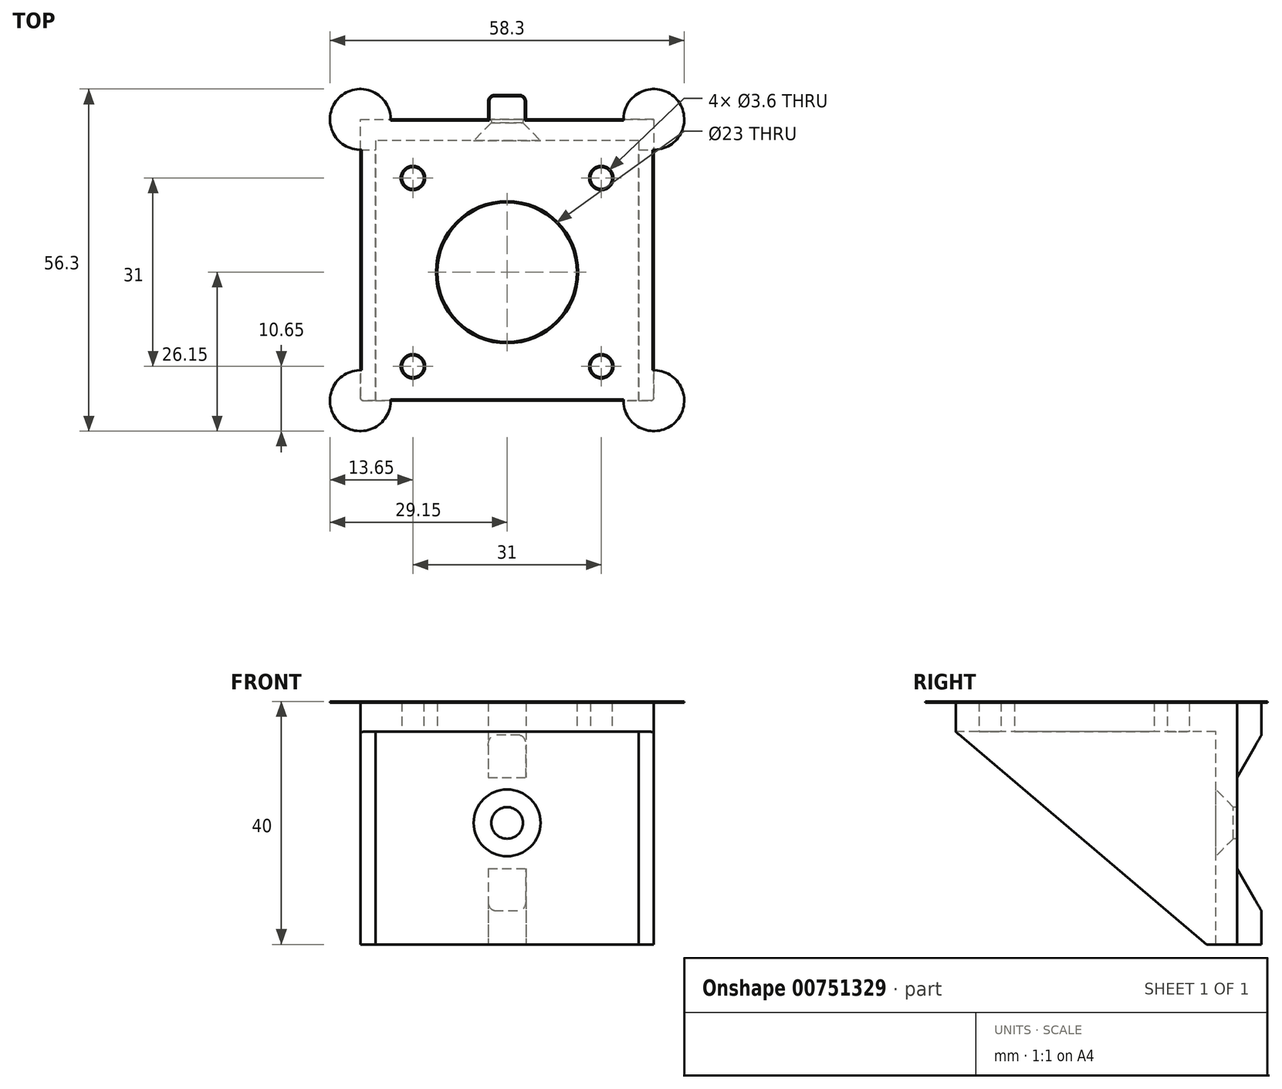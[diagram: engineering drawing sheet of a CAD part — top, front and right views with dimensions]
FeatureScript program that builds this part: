
annotation { "Feature Type Name" : "Feature", "Feature Type Description" : "" }
export const myFeature = defineFeature(function(context is Context, id is Id, definition is map)
    precondition{}
    {
        {
            var Q0;
            Q0=qCreatedBy(makeId("Top.planeOp"),FACE);
            var sketch = newSketch(context, id + "F0", { "sketchPlane" : qUnion([Q0])});
            skLineSegment(sketch, "E0.bottom", {"start": v(15.5, 15.5) * mm, "end": v(-15.5, 15.5) * mm, "construction": true});
            skLineSegment(sketch, "E0.top", {"start": v(15.5, -15.5) * mm, "end": v(-15.5, -15.5) * mm, "construction": true});
            skLineSegment(sketch, "E0.left", {"start": v(15.5, 15.5) * mm, "end": v(15.5, -15.5) * mm, "construction": true});
            skLineSegment(sketch, "E0.right", {"start": v(-15.5, 15.5) * mm, "end": v(-15.5, -15.5) * mm, "construction": true});
            skPoint(sketch, "E0.middle", {"position": v(0, 0) * mm});
            skCircle(sketch, "E1", {"center": v(15.5, 15.5) * mm, "radius": 1.5 * mm, "construction": true});
            skCircle(sketch, "E2", {"center": v(15.5, -15.5) * mm, "radius": 1.5 * mm, "construction": true});
            skCircle(sketch, "E3", {"center": v(-15.5, -15.5) * mm, "radius": 1.5 * mm, "construction": true});
            skCircle(sketch, "E4", {"center": v(-15.5, 15.5) * mm, "radius": 1.5 * mm, "construction": true});
            skLineSegment(sketch, "E5.bottom", {"start": v(21.15, 21.15) * mm, "end": v(-21.15, 21.15) * mm, "construction": true});
            skLineSegment(sketch, "E5.top", {"start": v(21.15, -21.15) * mm, "end": v(-21.15, -21.15) * mm, "construction": true});
            skLineSegment(sketch, "E5.left", {"start": v(21.15, 21.15) * mm, "end": v(21.15, -21.15) * mm, "construction": true});
            skLineSegment(sketch, "E5.right", {"start": v(-21.15, 21.15) * mm, "end": v(-21.15, -21.15) * mm, "construction": true});
            skCircle(sketch, "E6", {"center": v(0, 0) * mm, "radius": 11 * mm, "construction": true});
            skSolve(sketch);
        }
        {
            var Q0;
            Q0=qCreatedBy(makeId("Top.planeOp"),FACE);
            var sketch = newSketch(context, id + "F1", { "sketchPlane" : qUnion([Q0])});
            skPoint(sketch, "E7.middle", {"position": v(0, 0) * mm});
            skLineSegment(sketch, "E8.0", {"start": v(-21.15, 21.15) * mm, "end": v(-21.15, -21.15) * mm, "construction": true});
            skLineSegment(sketch, "E9.0", {"start": v(21.15, 21.15) * mm, "end": v(-21.15, 21.15) * mm, "construction": true});
            skLineSegment(sketch, "E10.0", {"start": v(21.15, 21.15) * mm, "end": v(21.15, -21.15) * mm, "construction": true});
            skLineSegment(sketch, "E11.0", {"start": v(21.15, -21.15) * mm, "end": v(-21.15, -21.15) * mm, "construction": true});
            skLineSegment(sketch, "E12", {"start": v(-24.15, -21.15) * mm, "end": v(24.15, -21.15) * mm});
            skLineSegment(sketch, "E13", {"start": v(-24.15, -21.15) * mm, "end": v(-24.15, 25.15) * mm});
            skLineSegment(sketch, "E14", {"start": v(-24.15, 25.15) * mm, "end": v(24.15, 25.15) * mm});
            skLineSegment(sketch, "E15", {"start": v(24.15, 25.15) * mm, "end": v(24.15, -21.15) * mm});
            skLineSegment(sketch, "E16", {"start": v(-3.1, 25.15) * mm, "end": v(-3.1, 29.15) * mm});
            skLineSegment(sketch, "E17", {"start": v(-3.1, 29.15) * mm, "end": v(3.1, 29.15) * mm});
            skLineSegment(sketch, "E18", {"start": v(3.1, 29.15) * mm, "end": v(3.1, 25.15) * mm});
            skSolve(sketch);
        }
        {
            var Q0;
            Q0 = qSketchRegion(id + "F1", true);
            extrude(context, id + "F2", {"entities" : qUnion([Q0]), "depth" : 5 * mm, "offsetDistance" : 25 * mm, "hasSecondDirection" : true, "secondDirectionOppositeDirection" : true, "secondDirectionDepth" : 35 * mm});
        }
        {
            var Q0;
            Q0=makeQuery(id+"F2.opExtrude","SWEPT_EDGE",EDGE,{"disambiguationData":[OSD([sQuery(id+"F1.wireOp",EDGE,"E16"),sQuery(id+"F1.wireOp",EDGE,"E17")])]});
            var Q1;
            Q1=makeQuery(id+"F2.opExtrude","SWEPT_EDGE",EDGE,{"disambiguationData":[OSD([sQuery(id+"F1.wireOp",EDGE,"E17"),sQuery(id+"F1.wireOp",EDGE,"E18")])]});
            fillet(context, id + "F3", {"entities" : qUnion([Q0, Q1]), "radius" : 1 * mm, "allowEdgeOverflow" : false});
        }
        {
            var Q0;
            Q0=qCreatedBy(makeId("Right.planeOp"),FACE);
            var sketch = newSketch(context, id + "F4", { "sketchPlane" : qUnion([Q0])});
            skLineSegment(sketch, "E19.0.0", {"start": v(25.15, -35) * mm, "end": v(-21.15, -35) * mm, "construction": true});
            skLineSegment(sketch, "E19.0.1", {"start": v(-21.15, -35) * mm, "end": v(-21.15, 5) * mm, "construction": true});
            skLineSegment(sketch, "E19.0.2", {"start": v(-21.15, 5) * mm, "end": v(25.15, 5) * mm, "construction": true});
            skLineSegment(sketch, "E19.0.3", {"start": v(25.15, 5) * mm, "end": v(25.15, -35) * mm, "construction": true});
            skLineSegment(sketch, "E20", {"start": v(-21.15, 0) * mm, "end": v(20.15, -35) * mm});
            skLineSegment(sketch, "E21", {"start": v(20.15, -35) * mm, "end": v(-21.15, -35) * mm});
            skLineSegment(sketch, "E22", {"start": v(-21.15, 0) * mm, "end": v(-21.15, -35) * mm});
            skPoint(sketch, "E23", {"position": v(25.15, -15) * mm});
            skLineSegment(sketch, "E24", {"start": v(25.15, -7.5) * mm, "end": v(25.15, -22.5) * mm});
            skLineSegment(sketch, "E25", {"start": v(25.15, -7.5) * mm, "end": v(34.92, 9.42) * mm});
            skLineSegment(sketch, "E26", {"start": v(34.92, 9.42) * mm, "end": v(34.92, -39.42) * mm});
            skLineSegment(sketch, "E27", {"start": v(34.92, -39.42) * mm, "end": v(25.15, -22.5) * mm});
            skSolve(sketch);
        }
        {
            var Q0;
            Q0 = qSketchRegion(id + "F4", true);
            extrude(context, id + "F5", {"entities" : qUnion([Q0]), "operationType" : NewBodyOperationType.REMOVE, "endBound" : BoundingType.THROUGH_ALL, "oppositeDirection" : true, "depth" : 25 * mm, "offsetDistance" : 25 * mm, "hasSecondDirection" : true, "secondDirectionBound" : BoundingType.THROUGH_ALL, "secondDirectionOppositeDirection" : false, "secondDirectionDepth" : 25 * mm});
        }
        {
            var Q0;
            Q0=qCreatedBy(makeId("Top.planeOp"),FACE);
            var sketch = newSketch(context, id + "F6", { "sketchPlane" : qUnion([Q0])});
            skLineSegment(sketch, "E28.0", {"start": v(21.65, 21.65) * mm, "end": v(-21.65, 21.65) * mm});
            skLineSegment(sketch, "E28.1", {"start": v(21.65, 21.65) * mm, "end": v(21.65, -21.65) * mm});
            skLineSegment(sketch, "E28.2", {"start": v(21.65, -21.65) * mm, "end": v(-21.65, -21.65) * mm});
            skLineSegment(sketch, "E28.3", {"start": v(-21.65, 21.65) * mm, "end": v(-21.65, -21.65) * mm});
            skCircle(sketch, "E29.0", {"center": v(15.5, 15.5) * mm, "radius": 1.8 * mm});
            skCircle(sketch, "E30.0", {"center": v(-15.5, 15.5) * mm, "radius": 1.8 * mm});
            skCircle(sketch, "E31.0", {"center": v(-15.5, -15.5) * mm, "radius": 1.8 * mm});
            skCircle(sketch, "E32.0", {"center": v(15.5, -15.5) * mm, "radius": 1.8 * mm});
            skCircle(sketch, "E33.0", {"center": v(0, 0) * mm, "radius": 11.5 * mm});
            skSolve(sketch);
        }
        {
            var Q0;
            Q0=makeQuery(id+"F6.imprint","IMPRINT",FACE,{"disambiguationData":[TD([[makeQuery(id+"F6.imprint","IMPRINT",EDGE,{"derivedFrom":sQuery(id+"F6.wireOp",EDGE,"E28.0")}),1.0]])]});
            var Q1;
            Q1=makeQuery(id+"F6.imprint","IMPRINT",FACE,{"disambiguationData":[TD([[makeQuery(id+"F6.imprint","IMPRINT",EDGE,{"derivedFrom":sQuery(id+"F6.wireOp",EDGE,"E31.0")}),1.0]])]});
            var Q2;
            Q2=makeQuery(id+"F6.imprint","IMPRINT",FACE,{"disambiguationData":[TD([[makeQuery(id+"F6.imprint","IMPRINT",EDGE,{"derivedFrom":sQuery(id+"F6.wireOp",EDGE,"E30.0")}),1.0]])]});
            var Q3;
            Q3=makeQuery(id+"F6.imprint","IMPRINT",FACE,{"disambiguationData":[TD([[makeQuery(id+"F6.imprint","IMPRINT",EDGE,{"derivedFrom":sQuery(id+"F6.wireOp",EDGE,"E33.0")}),1.0]])]});
            var Q4;
            Q4=makeQuery(id+"F6.imprint","IMPRINT",FACE,{"disambiguationData":[TD([[makeQuery(id+"F6.imprint","IMPRINT",EDGE,{"derivedFrom":sQuery(id+"F6.wireOp",EDGE,"E29.0")}),1.0]])]});
            var Q5;
            Q5=makeQuery(id+"F6.imprint","IMPRINT",FACE,{"disambiguationData":[TD([[makeQuery(id+"F6.imprint","IMPRINT",EDGE,{"derivedFrom":sQuery(id+"F6.wireOp",EDGE,"E32.0")}),1.0]])]});
            extrude(context, id + "F7", {"entities" : qUnion([Q0, Q1, Q2, Q3, Q4, Q5]), "operationType" : NewBodyOperationType.REMOVE, "endBound" : BoundingType.THROUGH_ALL, "oppositeDirection" : true, "depth" : 25 * mm, "offsetDistance" : 25 * mm});
        }
        {
            var Q0;
            Q0=makeQuery(id+"F6.imprint","IMPRINT",FACE,{"disambiguationData":[TD([[makeQuery(id+"F6.imprint","IMPRINT",EDGE,{"derivedFrom":sQuery(id+"F6.wireOp",EDGE,"E33.0")}),1.0]])]});
            var Q1;
            Q1=makeQuery(id+"F6.imprint","IMPRINT",FACE,{"disambiguationData":[TD([[makeQuery(id+"F6.imprint","IMPRINT",EDGE,{"derivedFrom":sQuery(id+"F6.wireOp",EDGE,"E31.0")}),1.0]])]});
            var Q2;
            Q2=makeQuery(id+"F6.imprint","IMPRINT",FACE,{"disambiguationData":[TD([[makeQuery(id+"F6.imprint","IMPRINT",EDGE,{"derivedFrom":sQuery(id+"F6.wireOp",EDGE,"E32.0")}),1.0]])]});
            var Q3;
            Q3=makeQuery(id+"F6.imprint","IMPRINT",FACE,{"disambiguationData":[TD([[makeQuery(id+"F6.imprint","IMPRINT",EDGE,{"derivedFrom":sQuery(id+"F6.wireOp",EDGE,"E29.0")}),1.0]])]});
            var Q4;
            Q4=makeQuery(id+"F6.imprint","IMPRINT",FACE,{"disambiguationData":[TD([[makeQuery(id+"F6.imprint","IMPRINT",EDGE,{"derivedFrom":sQuery(id+"F6.wireOp",EDGE,"E30.0")}),1.0]])]});
            extrude(context, id + "F8", {"entities" : qUnion([Q0, Q1, Q2, Q3, Q4]), "operationType" : NewBodyOperationType.REMOVE, "endBound" : BoundingType.THROUGH_ALL, "depth" : 25 * mm, "offsetDistance" : 25 * mm});
        }
        {
            var Q0;
            Q0=qCreatedBy(makeId("Right.planeOp"),FACE);
            var sketch = newSketch(context, id + "F9", { "sketchPlane" : qUnion([Q0])});
            skPoint(sketch, "E34.0", {"position": v(25.15, -15) * mm});
            skLineSegment(sketch, "E35", {"start": v(25.15, -15) * mm, "end": v(25.15, -17.6) * mm});
            skLineSegment(sketch, "E36", {"start": v(25.15, -17.6) * mm, "end": v(24.55, -17.6) * mm});
            skLineSegment(sketch, "E37", {"start": v(24.55, -17.6) * mm, "end": v(21.65, -20.5) * mm});
            skLineSegment(sketch, "E38", {"start": v(21.65, -20.5) * mm, "end": v(21.65, -15) * mm});
            skLineSegment(sketch, "E39", {"start": v(25.15, -15) * mm, "end": v(21.65, -15) * mm});
            skLineSegment(sketch, "E40.0.0", {"start": v(21.65, -35) * mm, "end": v(21.65, 0) * mm, "construction": true});
            skLineSegment(sketch, "E40.0.2", {"start": v(21.65, 0) * mm, "end": v(21.65, -35) * mm, "construction": true});
            skSolve(sketch);
        }
        {
            var Q0;
            Q0=makeQuery(id+"F9.imprint","IMPRINT",FACE,{"disambiguationData":[TD([[makeQuery(id+"F9.imprint","IMPRINT",EDGE,{"derivedFrom":sQuery(id+"F9.wireOp",EDGE,"E35")}),-1.0]])]});
            var Q1;
            Q1=sQuery(id+"F9.wireOp",EDGE,"E39");
            revolve(context, id + "F10", {"operationType" : NewBodyOperationType.REMOVE, "surfaceOperationType" : NewSurfaceOperationType.NEW, "entities" : qUnion([Q0]), "axis" : qUnion([Q1]), "revolveType" : RevolveType.FULL, "oppositeDirection" : true});
        }
        {
            var Q0;
            Q0=makeQuery(id+"F2.opExtrude","CAP_FACE",FACE,{"disambiguationData":[OSD([sQuery(id+"F1.wireOp",EDGE,"E12"),sQuery(id+"F1.wireOp",EDGE,"E13"),sQuery(id+"F1.wireOp",EDGE,"E14"),sQuery(id+"F1.wireOp",EDGE,"E15"),sQuery(id+"F1.wireOp",EDGE,"E16"),sQuery(id+"F1.wireOp",EDGE,"E17"),sQuery(id+"F1.wireOp",EDGE,"E18")])],"isStart":false});
            var sketch = newSketch(context, id + "F11", { "sketchPlane" : qUnion([Q0])});
            skCircle(sketch, "E41", {"center": v(24.15, 25.15) * mm, "radius": 5 * mm});
            skCircle(sketch, "E42", {"center": v(24.15, -21.15) * mm, "radius": 5 * mm});
            skCircle(sketch, "E43", {"center": v(-24.15, -21.15) * mm, "radius": 5 * mm});
            skCircle(sketch, "E44", {"center": v(-24.15, 25.15) * mm, "radius": 5 * mm});
            skSolve(sketch);
        }
        {
            var Q0;
            Q0=makeQuery(id+"F2.opExtrude","SWEPT_EDGE",EDGE,{"disambiguationData":[OSD([sQuery(id+"F1.wireOp",EDGE,"E14"),sQuery(id+"F1.wireOp",EDGE,"E15")])]});
            var Q1;
            Q1=makeQuery(id+"F2.opExtrude","SWEPT_EDGE",EDGE,{"disambiguationData":[OSD([sQuery(id+"F1.wireOp",EDGE,"E13"),sQuery(id+"F1.wireOp",EDGE,"E14")])]});
            var Q2;
            Q2=makeQuery(id+"F2.opExtrude","SWEPT_EDGE",EDGE,{"disambiguationData":[OSD([sQuery(id+"F1.wireOp",EDGE,"E12"),sQuery(id+"F1.wireOp",EDGE,"E13")])]});
            var Q3;
            Q3=makeQuery(id+"F2.opExtrude","SWEPT_EDGE",EDGE,{"disambiguationData":[OSD([sQuery(id+"F1.wireOp",EDGE,"E12"),sQuery(id+"F1.wireOp",EDGE,"E15")])]});
            fillet(context, id + "F12", {"entities" : qUnion([Q0, Q1, Q2, Q3]), "radius" : 0.5 * mm, "allowEdgeOverflow" : false});
        }
        {
            var Q0;
            Q0=makeQuery(id+"F2.opExtrude","CAP_FACE",FACE,{"disambiguationData":[OSD([sQuery(id+"F1.wireOp",EDGE,"E12"),sQuery(id+"F1.wireOp",EDGE,"E13"),sQuery(id+"F1.wireOp",EDGE,"E14"),sQuery(id+"F1.wireOp",EDGE,"E15"),sQuery(id+"F1.wireOp",EDGE,"E16"),sQuery(id+"F1.wireOp",EDGE,"E17"),sQuery(id+"F1.wireOp",EDGE,"E18")])],"isStart":false});
            chamfer(context, id + "F13", {"entities" : qUnion([Q0]), "width" : 0.2 * mm});
        }
        {
            var Q0;
            Q0 = qSketchRegion(id + "F11", true);
            extrude(context, id + "F14", {"entities" : qUnion([Q0]), "operationType" : NewBodyOperationType.ADD, "oppositeDirection" : true, "depth" : 0.2 * mm, "offsetDistance" : 25 * mm});
        }
    });
